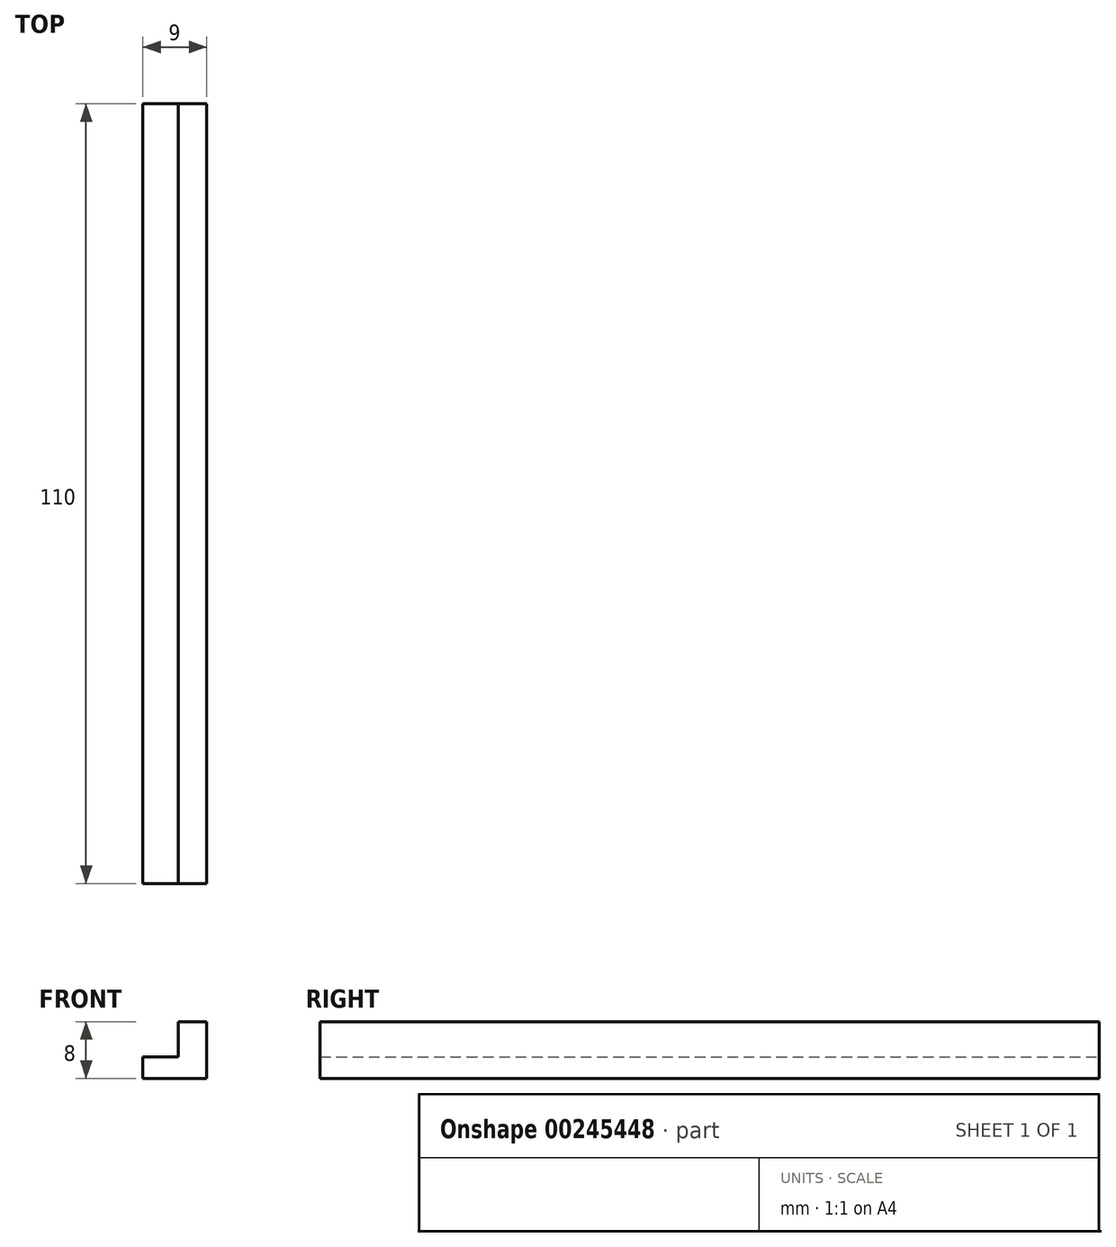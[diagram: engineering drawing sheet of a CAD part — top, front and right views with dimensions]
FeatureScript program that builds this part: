
annotation { "Feature Type Name" : "Feature", "Feature Type Description" : "" }
export const myFeature = defineFeature(function(context is Context, id is Id, definition is map)
    precondition{}
    {
        {
            var Q0;
            Q0=qCreatedBy(makeId("Front.planeOp"),FACE);
            var sketch = newSketch(context, id + "F0", { "sketchPlane" : qUnion([Q0])});
            skLineSegment(sketch, "E0", {"start": v(0, 0) * mm, "end": v(0, 3) * mm});
            skLineSegment(sketch, "E1", {"start": v(0, 3) * mm, "end": v(5, 3) * mm});
            skLineSegment(sketch, "E2", {"start": v(5, 3) * mm, "end": v(5, 8) * mm});
            skLineSegment(sketch, "E3", {"start": v(5, 8) * mm, "end": v(9, 8) * mm});
            skLineSegment(sketch, "E4", {"start": v(9, 8) * mm, "end": v(9, 0) * mm});
            skLineSegment(sketch, "E5", {"start": v(9, 0) * mm, "end": v(0, 0) * mm});
            skSolve(sketch);
        }
        {
            var Q0;
            Q0=qSketchRegion(id+"F0",true);
            extrude(context, id + "F1", {"entities" : qUnion([Q0]), "depth" : 110 * mm});
        }
    });
